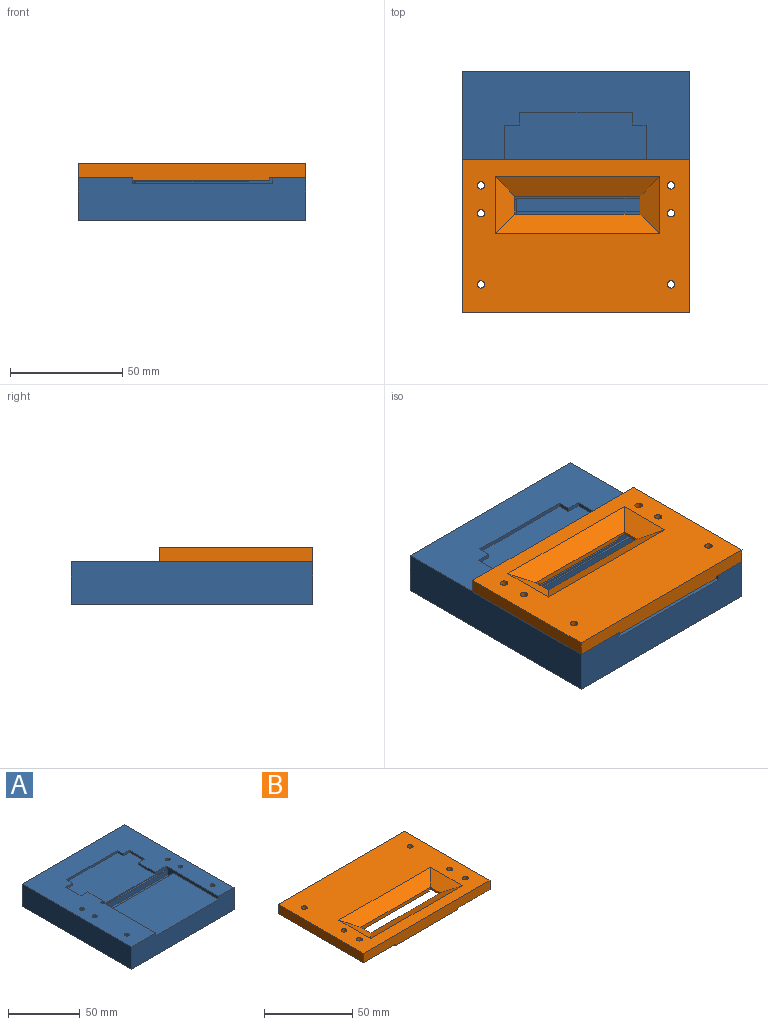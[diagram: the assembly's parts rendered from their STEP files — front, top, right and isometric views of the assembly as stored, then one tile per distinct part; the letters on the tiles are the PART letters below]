
ASSEMBLY  parts=2 mates=1
PART A: 33 faces, bbox 101.6x108x19.1 mm
  f0: plane 62.47x45.07mm, normal (0,0,1), area 2815.5mm2, adj f7,f11,f12,f24
  f1: plane 107.95x101.6mm, normal (0,0,1), area 5581.8mm2, adj f2,f3,f4,f5,f6,f7,f8,f10
  f2: plane 5.72x1.8mm, normal (1,0,0), area 10.3mm2, adj f1,f16,f17,f21
  f3: plane 5.72x1.8mm, normal (-1,0,0), area 10.3mm2, adj f1,f16,f17,f18
  f4: plane 61.04x2.6mm, normal (0,-1,0), area 68.4mm2, adj f1,f10,f12,f13,f14,f15,f17
  f5: plane 101.6x19.05mm, normal (0,1,0), area 1935.5mm2, adj f1,f6,f8,f9
  f6: plane 107.95x19.05mm, normal (-1,0,0), area 2056.4mm2, adj f1,f5,f7,f9
  f7: plane 101.6x19.05mm, normal (0,-1,0), area 1773.1mm2, adj f0,f1,f6,f8,f9,f11,f12
  f8: plane 107.95x19.05mm, normal (1,0,0), area 2056.4mm2, adj f1,f5,f7,f9
  f9: plane 107.95x101.6mm, normal (0,0,-1), area 10916.4mm2, adj f5,f6,f7,f8,f27,f28,f29,f30
  f10: cylinder r=1.43mm len=2.85mm, axis (0,0,1), area 17.5mm2, adj f1,f4,f11,f13
  f11: plane 51.07x7mm, normal (1,0,0), area 158.1mm2, adj f0,f1,f7,f10,f13,f24,f25,f26
  f12: plane 52.07x7mm, normal (-1,0,0), area 161.8mm2, adj f0,f1,f4,f7,f13,f24,f25,f26
  f13: plane 63.9x2.85mm, normal (0,0,1), area 67.3mm2, adj f4,f10,f11,f12,f25
  f14: plane 16.51x1.8mm, normal (1,0,0), area 29.7mm2, adj f1,f4,f17,f23
  f15: plane 16.51x1.8mm, normal (-1,0,0), area 29.7mm2, adj f1,f4,f17,f19
  f16: plane 50.17x1.8mm, normal (0,-1,0), area 90.3mm2, adj f1,f2,f3,f17
  f17: plane 63.13x37.47mm, normal (0,0,1), area 2077mm2, adj f2,f3,f4,f14,f15,f16,f18,f19
  f18: plane 6.24x1.8mm, normal (0,-1,0), area 11.2mm2, adj f1,f3,f17,f20
  f19: plane 6.24x1.8mm, normal (0,1,0), area 11.2mm2, adj f1,f15,f17,f20
  f20: plane 15.24x1.8mm, normal (-1,0,0), area 27.4mm2, adj f1,f17,f18,f19
  f21: plane 6.72x1.8mm, normal (0,-1,0), area 12.1mm2, adj f1,f2,f17,f22
  f22: plane 15.24x1.8mm, normal (1,0,0), area 27.4mm2, adj f1,f17,f21,f23
  f23: plane 6.72x1.8mm, normal (0,1,0), area 12.1mm2, adj f1,f14,f17,f22
  f24: plane 62.47x4.4mm, normal (0,1,0), area 274.9mm2, adj f0,f11,f12,f26
  f25: plane 62.47x4.4mm, normal (0,-1,0), area 274.9mm2, adj f11,f12,f13,f26
  f26: plane 62.47x6mm, normal (0,0,1), area 374.8mm2, adj f11,f12,f24,f25
  f27: cylinder r=1.65mm len=19.05mm, axis (0,0,1), area 197.5mm2, adj f1,f9
  f28: cylinder r=1.65mm len=19.05mm, axis (0,0,1), area 197.5mm2, adj f1,f9
  f29: cylinder r=1.65mm len=19.05mm, axis (0,0,1), area 197.5mm2, adj f1,f9
  f30: cylinder r=1.65mm len=19.05mm, axis (0,0,1), area 197.5mm2, adj f1,f9
  f31: cylinder r=1.65mm len=19.05mm, axis (0,0,1), area 197.5mm2, adj f1,f9
  f32: cylinder r=1.65mm len=19.05mm, axis (0,0,1), area 197.5mm2, adj f1,f9
PART B: 27 faces, bbox 101.6x68.3x7.4 mm
  f0: plane 68.33x25.73mm, normal (0,0,-1), area 1292.4mm2, adj f3,f4,f6,f7,f8,f14,f15,f16
  f1: plane 101.6x68.33mm, normal (0,0,1), area 5009.7mm2, adj f3,f4,f5,f10,f11,f12,f13,f14
  f2: plane 68.33x25.73mm, normal (0,0,-1), area 1649.6mm2, adj f3,f5,f6,f8,f9,f14,f17,f18
  f3: plane 101.6x7.35mm, normal (0,1,0), area 706.1mm2, adj f0,f1,f2,f4,f5,f21,f22,f23
  f4: plane 68.33x6.35mm, normal (-1,0,0), area 433.9mm2, adj f0,f1,f3,f14
  f5: plane 68.33x6.35mm, normal (1,0,0), area 433.9mm2, adj f1,f2,f3,f14
  f6: plane 55.88x2.27mm, normal (0,1,0), area 121.1mm2, adj f0,f2,f7,f9,f12,f24,f25,f26
  f7: plane 8x1.27mm, normal (1,0,0), area 10.2mm2, adj f0,f6,f8,f13
  f8: plane 61.72x2.27mm, normal (0,-1,0), area 131.9mm2, adj f0,f2,f7,f9,f11,f21,f22,f23
  f9: plane 8x1.27mm, normal (-1,0,0), area 10.2mm2, adj f2,f6,f8,f10
  f10: plane 25.6x8.8mm, normal (-0.5,0,0.87), area 170.7mm2, adj f1,f9,f11,f12
  f11: plane 73.48x8.8mm, normal (0,-0.5,0.87), area 657.1mm2, adj f1,f8,f10,f13
  f12: plane 73.48x8.8mm, normal (0,0.5,0.87), area 657.1mm2, adj f1,f6,f10,f13
  f13: plane 25.6x8.8mm, normal (0.5,0,0.87), area 170.7mm2, adj f1,f7,f11,f12
  f14: plane 101.6x7.35mm, normal (0,-1,0), area 695.3mm2, adj f0,f1,f2,f4,f5,f24,f25,f26
  f15: cylinder r=1.65mm len=6.35mm, axis (0,0,1), area 65.8mm2, adj f0,f1
  f16: cylinder r=1.65mm len=6.35mm, axis (0,0,1), area 65.8mm2, adj f0,f1
  f17: cylinder r=1.65mm len=6.35mm, axis (0,0,1), area 65.8mm2, adj f1,f2
  f18: cylinder r=1.65mm len=6.35mm, axis (0,0,1), area 65.8mm2, adj f1,f2
  f19: cylinder r=1.65mm len=6.35mm, axis (0,0,1), area 65.8mm2, adj f1,f2
  f20: cylinder r=1.65mm len=6.35mm, axis (0,0,1), area 65.8mm2, adj f0,f1
  f21: plane 44.07x1mm, normal (1,0,0), area 44.1mm2, adj f2,f3,f8,f23
  f22: plane 44.07x1mm, normal (-1,0,0), area 44.1mm2, adj f0,f3,f8,f23
  f23: plane 60.96x44.07mm, normal (0,0,-1), area 2686.5mm2, adj f3,f8,f21,f22
  f24: plane 16.26x1mm, normal (-1,0,0), area 16.3mm2, adj f0,f6,f14,f26
  f25: plane 16.26x1mm, normal (1,0,0), area 16.3mm2, adj f2,f6,f14,f26
  f26: plane 50.14x16.26mm, normal (0,0,-1), area 815.1mm2, adj f6,f14,f24,f25
PLACE A t=(-150.29,193.43,-225.43)mm
PLACE B rot(axis=(0,0,1),180deg) t=(-114.33,85.48,-206.38)mm
MATE planar B.f2 <-> A.f1  axis (0,0,-1) through (-159.62,137.55,-206.38)mm
